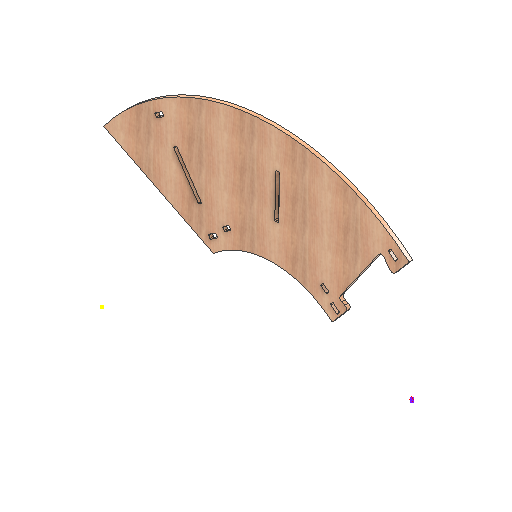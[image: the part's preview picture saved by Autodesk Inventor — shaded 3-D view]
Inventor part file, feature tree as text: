
AUTODESK INVENTOR PART (.ipt)
format: ipt  version: 2021 (Build 250183000, 183)  size: 512,000 bytes
history: native  units: mm
features: other x2, extrude x2, sketch x1, hole x1
ambient origin geometry x8: Origin, YZ Plane, XZ Plane, XY Plane, X Axis, Y Axis, Z Axis, Center Point
bodies: Body1 (feature_tree)
feature tree (6):
  sketch  "Sketch1"  dims[d1=30.0mm d3=179.25mm d5=149.25mm d7=358.5mm d9=1031.078896mm d11=450.101934mm d13=122.534166mm d15=116.345829mm d17=116.323394mm d19=19.0mm d21=122.511376mm d23=30.0mm d25=36.0mm d27=6.283185mm d29=5.061454mm d31=18.0mm d33=18.0mm d35=60.0mm d42=18.0mm d43=0.0mm d44=18.0mm d45=0.0mm]
  other  "CONTOURS"
  hole  "HOLES"  [1 undecoded]
  other  "LETTERS"
  extrude  "Extrusion4"  Depth=18.0mm
  extrude  "Extrusion5"  Depth=18.0mm
note: 1 required parameter value undecoded (feature->parameter linkage not recoverable at this tier; creation-order binding heuristic only, values carry confidence <= 0.55)
